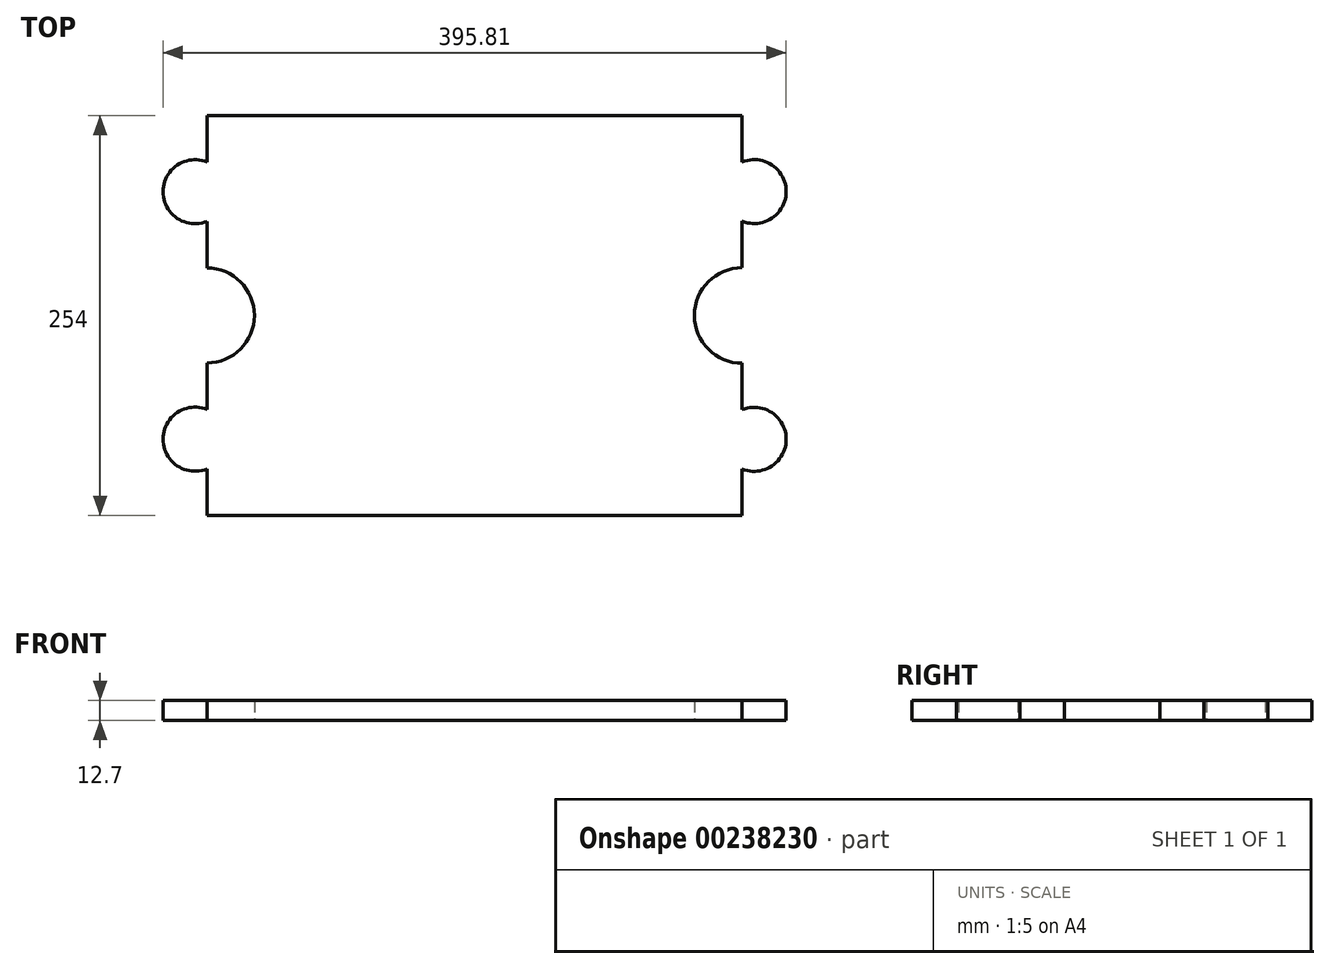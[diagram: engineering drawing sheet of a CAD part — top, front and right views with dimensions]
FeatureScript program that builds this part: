
annotation { "Feature Type Name" : "Feature", "Feature Type Description" : "" }
export const myFeature = defineFeature(function(context is Context, id is Id, definition is map)
    precondition{}
    {
        {
            var Q0;
            Q0=qCreatedBy(makeId("Top.planeOp"),FACE);
            var sketch = newSketch(context, id + "F0", { "sketchPlane" : qUnion([Q0])});
            skPoint(sketch, "E0.endSnap0", {"position": v(279.4, 76.2) * mm});
            skArc(sketch, "E1", {"start": v(-30.18, 46.02) * mm, "mid": v(0, 76.2) * mm, "end": v(-30.18, 106.38) * mm});
            skArc(sketch, "E2", {"start": v(309.75, 106.55) * mm, "mid": v(279.4, 76.2) * mm, "end": v(309.75, 45.85) * mm});
            skLineSegment(sketch, "E3", {"start": v(-30.18, 106.38) * mm, "end": v(-30.18, 135.95) * mm});
            skLineSegment(sketch, "E4", {"start": v(309.75, 106.55) * mm, "end": v(309.75, 136.04) * mm});
            skLineSegment(sketch, "E5", {"start": v(309.75, 203.2) * mm, "end": v(-30.18, 203.2) * mm});
            skLineSegment(sketch, "E6.MirrorCS", {"start": v(309.75, -50.8) * mm, "end": v(-30.18, -50.8) * mm});
            skArc(sketch, "E7", {"start": v(-30.18, 173.62) * mm, "mid": v(-58.12, 154.79) * mm, "end": v(-30.18, 135.95) * mm});
            skArc(sketch, "E8", {"start": v(309.75, 136.04) * mm, "mid": v(337.7, 154.88) * mm, "end": v(309.75, 173.71) * mm});
            skLineSegment(sketch, "E9.MirrorCS", {"start": v(-30.18, 46.02) * mm, "end": v(-30.18, 16.45) * mm});
            skArc(sketch, "E10.MirrorC", {"start": v(-30.18, -21.22) * mm, "mid": v(-58.12, -2.39) * mm, "end": v(-30.18, 16.45) * mm});
            skArc(sketch, "E11.MirrorC", {"start": v(309.75, 16.36) * mm, "mid": v(337.7, -2.48) * mm, "end": v(309.75, -21.31) * mm});
            skLineSegment(sketch, "E12.MirrorCS", {"start": v(309.75, 45.85) * mm, "end": v(309.75, 16.36) * mm});
            skLineSegment(sketch, "E13.trimOffspring", {"start": v(309.75, -21.31) * mm, "end": v(309.75, -50.8) * mm});
            skLineSegment(sketch, "E14.trimOffspring", {"start": v(-30.18, -21.22) * mm, "end": v(-30.18, -50.8) * mm});
            skLineSegment(sketch, "E15.trimOffspring", {"start": v(-30.18, 173.62) * mm, "end": v(-30.18, 203.2) * mm});
            skLineSegment(sketch, "E16.trimOffspring", {"start": v(309.75, 173.71) * mm, "end": v(309.75, 203.2) * mm});
            skSolve(sketch);
        }
        {
            var Q0;
            Q0=makeQuery(id+"F0.imprint","IMPRINT",FACE,{"disambiguationData":[TD([[makeQuery(id+"F0.imprint","IMPRINT",EDGE,{"derivedFrom":sQuery(id+"F0.wireOp",EDGE,"E1")}),-1.0]])]});
            extrude(context, id + "F1", {"entities" : qUnion([Q0]), "depth" : 12.7 * mm});
        }
    });
